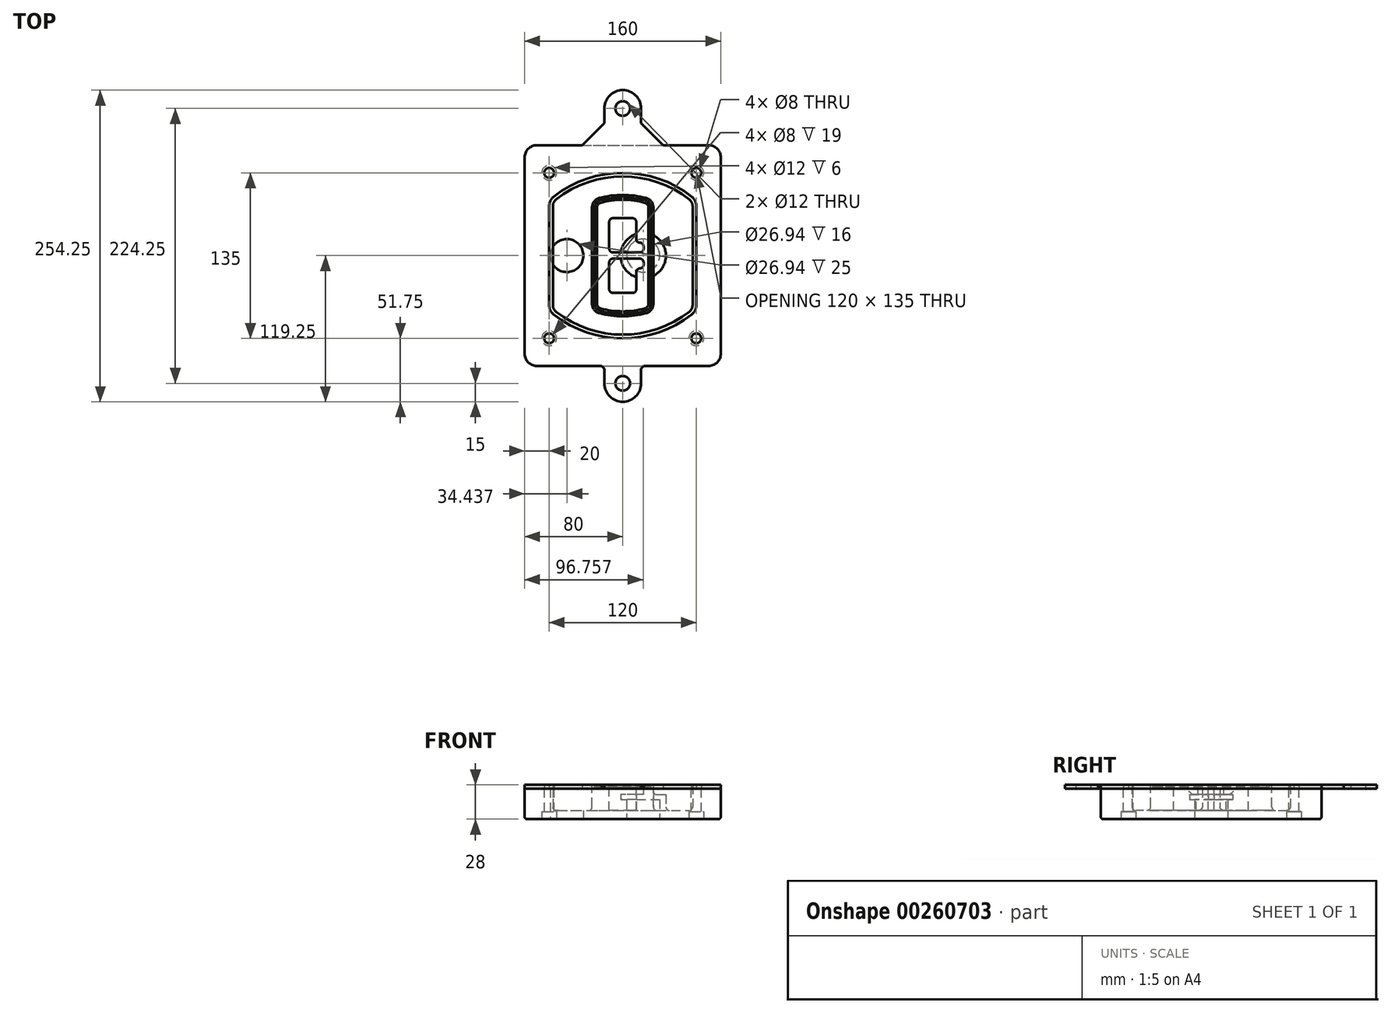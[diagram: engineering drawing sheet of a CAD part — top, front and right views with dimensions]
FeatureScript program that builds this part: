
annotation { "Feature Type Name" : "Feature", "Feature Type Description" : "" }
export const myFeature = defineFeature(function(context is Context, id is Id, definition is map)
    precondition{}
    {
        {
            var Q0;
            Q0=qCreatedBy(makeId("Top.planeOp"),FACE);
            var sketch = newSketch(context, id + "F0", { "sketchPlane" : qUnion([Q0])});
            skPoint(sketch, "E0.rect.middle", {"position": v(0, 0) * mm});
            skLineSegment(sketch, "E1.bottom", {"start": v(-70, -90) * mm, "end": v(70, -90) * mm});
            skLineSegment(sketch, "E1.top", {"start": v(-70, 90) * mm, "end": v(70, 90) * mm});
            skLineSegment(sketch, "E1.left", {"start": v(-80, -80) * mm, "end": v(-80, 80) * mm});
            skLineSegment(sketch, "E1.right", {"start": v(80, -80) * mm, "end": v(80, 80) * mm});
            skLineSegment(sketch, "E2", {"start": v(-80, 90) * mm, "end": v(80, -90) * mm, "construction": true});
            skLineSegment(sketch, "E3", {"start": v(80, 90) * mm, "end": v(-80, -90) * mm, "construction": true});
            skCircle(sketch, "E4", {"center": v(-60, 67.5) * mm, "radius": 4 * mm});
            skCircle(sketch, "E5", {"center": v(60, 67.5) * mm, "radius": 4 * mm});
            skCircle(sketch, "E6", {"center": v(60, -67.5) * mm, "radius": 4 * mm});
            skCircle(sketch, "E7", {"center": v(-60, -67.5) * mm, "radius": 4 * mm});
            skLineSegment(sketch, "E8", {"start": v(-60, 67.5) * mm, "end": v(60, 67.5) * mm, "construction": true});
            skLineSegment(sketch, "E9", {"start": v(60, 67.5) * mm, "end": v(60, -67.5) * mm, "construction": true});
            skLineSegment(sketch, "E10", {"start": v(60, -67.5) * mm, "end": v(-60, -67.5) * mm, "construction": true});
            skLineSegment(sketch, "E11", {"start": v(-60, -67.5) * mm, "end": v(-60, 67.5) * mm, "construction": true});
            skLineSegment(sketch, "E12", {"start": v(-60, 40.3) * mm, "end": v(-60, -40.3) * mm});
            skLineSegment(sketch, "E13", {"start": v(60, 40.3) * mm, "end": v(60, -40.3) * mm});
            skArc(sketch, "E14", {"start": v(56.15, 48.18) * mm, "mid": v(0, 67.5) * mm, "end": v(-56.15, 48.18) * mm});
            skArc(sketch, "E15", {"start": v(-56.15, -48.18) * mm, "mid": v(0, -67.5) * mm, "end": v(56.15, -48.18) * mm});
            skLineSegment(sketch, "E16", {"start": v(-60, 0) * mm, "end": v(60, 0) * mm, "construction": true});
            skPoint(sketch, "E17.visualSharp", {"position": v(-60, -45) * mm});
            skArc(sketch, "E17.filletArc", {"start": v(-60, -40.3) * mm, "mid": v(-58.99, -44.68) * mm, "end": v(-56.15, -48.18) * mm});
            skPoint(sketch, "E18.visualSharp", {"position": v(-60, 45) * mm});
            skArc(sketch, "E18.filletArc", {"start": v(-56.15, 48.18) * mm, "mid": v(-58.99, 44.68) * mm, "end": v(-60, 40.3) * mm});
            skPoint(sketch, "E19.visualSharp", {"position": v(60, 45) * mm});
            skArc(sketch, "E19.filletArc", {"start": v(60, 40.3) * mm, "mid": v(58.99, 44.68) * mm, "end": v(56.15, 48.18) * mm});
            skPoint(sketch, "E20.visualSharp", {"position": v(60, -45) * mm});
            skArc(sketch, "E20.filletArc", {"start": v(56.15, -48.18) * mm, "mid": v(58.99, -44.68) * mm, "end": v(60, -40.3) * mm});
            skPoint(sketch, "E21.visualSharp", {"position": v(-80, 90) * mm});
            skArc(sketch, "E21.filletArc", {"start": v(-70, 90) * mm, "mid": v(-77.07, 87.07) * mm, "end": v(-80, 80) * mm});
            skPoint(sketch, "E22.visualSharp", {"position": v(80, 90) * mm});
            skArc(sketch, "E22.filletArc", {"start": v(80, 80) * mm, "mid": v(77.07, 87.07) * mm, "end": v(70, 90) * mm});
            skPoint(sketch, "E23.visualSharp", {"position": v(80, -90) * mm});
            skArc(sketch, "E23.filletArc", {"start": v(70, -90) * mm, "mid": v(77.07, -87.07) * mm, "end": v(80, -80) * mm});
            skPoint(sketch, "E24.visualSharp", {"position": v(-80, -90) * mm});
            skArc(sketch, "E24.filletArc", {"start": v(-80, -80) * mm, "mid": v(-77.07, -87.07) * mm, "end": v(-70, -90) * mm});
            skArc(sketch, "E25.0", {"start": v(57, 40.3) * mm, "mid": v(56.3, 43.36) * mm, "end": v(54.3, 45.81) * mm});
            skLineSegment(sketch, "E25.1", {"start": v(57, 40.3) * mm, "end": v(57, -40.3) * mm});
            skArc(sketch, "E25.2", {"start": v(54.3, -45.81) * mm, "mid": v(56.3, -43.36) * mm, "end": v(57, -40.3) * mm});
            skArc(sketch, "E25.3", {"start": v(-54.3, -45.81) * mm, "mid": v(0, -64.5) * mm, "end": v(54.3, -45.81) * mm});
            skArc(sketch, "E25.4", {"start": v(-57, -40.3) * mm, "mid": v(-56.3, -43.36) * mm, "end": v(-54.3, -45.81) * mm});
            skArc(sketch, "E25.5", {"start": v(54.3, 45.81) * mm, "mid": v(0, 64.5) * mm, "end": v(-54.3, 45.81) * mm});
            skLineSegment(sketch, "E25.6", {"start": v(-57, 40.3) * mm, "end": v(-57, -40.3) * mm});
            skArc(sketch, "E25.7", {"start": v(-54.3, 45.81) * mm, "mid": v(-56.3, 43.36) * mm, "end": v(-57, 40.3) * mm});
            skArc(sketch, "E26.0", {"start": v(-58.62, 51.33) * mm, "mid": v(-62.58, 46.43) * mm, "end": v(-64, 40.3) * mm});
            skArc(sketch, "E26.1", {"start": v(58.62, 51.33) * mm, "mid": v(0, 71.5) * mm, "end": v(-58.62, 51.33) * mm});
            skArc(sketch, "E26.2", {"start": v(64, 40.3) * mm, "mid": v(62.58, 46.43) * mm, "end": v(58.62, 51.33) * mm});
            skLineSegment(sketch, "E26.3", {"start": v(64, 40.3) * mm, "end": v(64, -40.3) * mm});
            skArc(sketch, "E26.4", {"start": v(58.62, -51.33) * mm, "mid": v(62.58, -46.43) * mm, "end": v(64, -40.3) * mm});
            skLineSegment(sketch, "E26.5", {"start": v(-64, 40.3) * mm, "end": v(-64, -40.3) * mm});
            skArc(sketch, "E26.6", {"start": v(-58.62, -51.33) * mm, "mid": v(0, -71.5) * mm, "end": v(58.62, -51.33) * mm});
            skArc(sketch, "E26.7", {"start": v(-64, -40.3) * mm, "mid": v(-62.58, -46.43) * mm, "end": v(-58.62, -51.33) * mm});
            skSolve(sketch);
        }
        {
            var Q0;
            Q0=makeQuery(id+"F0.imprint","IMPRINT",FACE,{"disambiguationData":[TD([[makeQuery(id+"F0.imprint","IMPRINT",EDGE,{"derivedFrom":sQuery(id+"F0.wireOp",EDGE,"E1.bottom")}),1.0]])]});
            var Q1;
            Q1=makeQuery(id+"F0.imprint","IMPRINT",FACE,{"disambiguationData":[TD([[makeQuery(id+"F0.imprint","IMPRINT",EDGE,{"derivedFrom":sQuery(id+"F0.wireOp",EDGE,"E12")}),1.0]])]});
            var Q2;
            Q2=makeQuery(id+"F0.imprint","IMPRINT",FACE,{"disambiguationData":[TD([[makeQuery(id+"F0.imprint","IMPRINT",EDGE,{"derivedFrom":sQuery(id+"F0.wireOp",EDGE,"E25.0")}),1.0]])]});
            var Q3;
            Q3=makeQuery(id+"F0.imprint","IMPRINT",FACE,{"disambiguationData":[TD([[makeQuery(id+"F0.imprint","IMPRINT",EDGE,{"derivedFrom":sQuery(id+"F0.wireOp",EDGE,"E12")}),-1.0]])]});
            extrude(context, id + "F1", {"entities" : qUnion([Q0, Q1, Q2, Q3]), "oppositeDirection" : true, "depth" : 25 * mm});
        }
        {
            var Q0;
            Q0=makeQuery(id+"F0.imprint","IMPRINT",FACE,{"disambiguationData":[TD([[makeQuery(id+"F0.imprint","IMPRINT",EDGE,{"derivedFrom":sQuery(id+"F0.wireOp",EDGE,"E12")}),1.0]])]});
            extrude(context, id + "F2", {"entities" : qUnion([Q0]), "operationType" : NewBodyOperationType.ADD, "depth" : 3 * mm});
        }
        {
            var Q0;
            Q0=makeQuery(id+"F0.imprint","IMPRINT",FACE,{"disambiguationData":[TD([[makeQuery(id+"F0.imprint","IMPRINT",EDGE,{"derivedFrom":sQuery(id+"F0.wireOp",EDGE,"E25.0")}),1.0]])]});
            extrude(context, id + "F3", {"entities" : qUnion([Q0]), "operationType" : NewBodyOperationType.REMOVE, "oppositeDirection" : true, "depth" : 18 * mm});
        }
        {
            var Q0;
            Q0=makeQuery(id+"F2.opExtrude","CAP_FACE",FACE,{"disambiguationData":[OSD([sQuery(id+"F0.wireOp",EDGE,"E12"),sQuery(id+"F0.wireOp",EDGE,"E13"),sQuery(id+"F0.wireOp",EDGE,"E14"),sQuery(id+"F0.wireOp",EDGE,"E15"),sQuery(id+"F0.wireOp",EDGE,"E17.filletArc"),sQuery(id+"F0.wireOp",EDGE,"E18.filletArc"),sQuery(id+"F0.wireOp",EDGE,"E19.filletArc"),sQuery(id+"F0.wireOp",EDGE,"E20.filletArc"),sQuery(id+"F0.wireOp",EDGE,"E25.0"),sQuery(id+"F0.wireOp",EDGE,"E25.1"),sQuery(id+"F0.wireOp",EDGE,"E25.2"),sQuery(id+"F0.wireOp",EDGE,"E25.3"),sQuery(id+"F0.wireOp",EDGE,"E25.4"),sQuery(id+"F0.wireOp",EDGE,"E25.5"),sQuery(id+"F0.wireOp",EDGE,"E25.6"),sQuery(id+"F0.wireOp",EDGE,"E25.7")])],"isStart":false});
            var sketch = newSketch(context, id + "F4", { "sketchPlane" : qUnion([Q0])});
            skArc(sketch, "E27.0", {"start": v(-19.08, -46.97) * mm, "mid": v(0, -49.5) * mm, "end": v(19.08, -46.97) * mm});
            skArc(sketch, "E28.0", {"start": v(19.08, 46.97) * mm, "mid": v(0, 49.5) * mm, "end": v(-19.08, 46.97) * mm});
            skLineSegment(sketch, "E29", {"start": v(-25, 39.25) * mm, "end": v(-25, -39.25) * mm});
            skLineSegment(sketch, "E30", {"start": v(25, 39.25) * mm, "end": v(25, -39.25) * mm});
            skLineSegment(sketch, "E31", {"start": v(-25, 45.1) * mm, "end": v(25, 45.1) * mm, "construction": true});
            skLineSegment(sketch, "E32", {"start": v(-25, -45.1) * mm, "end": v(25, -45.1) * mm, "construction": true});
            skPoint(sketch, "E33.visualSharp", {"position": v(-25, 45.1) * mm});
            skArc(sketch, "E33.filletArc", {"start": v(-19.08, 46.97) * mm, "mid": v(-23.35, 44.11) * mm, "end": v(-25, 39.25) * mm});
            skPoint(sketch, "E34.visualSharp", {"position": v(25, 45.1) * mm});
            skArc(sketch, "E34.filletArc", {"start": v(25, 39.25) * mm, "mid": v(23.35, 44.11) * mm, "end": v(19.08, 46.97) * mm});
            skPoint(sketch, "E35.visualSharp", {"position": v(25, -45.1) * mm});
            skArc(sketch, "E35.filletArc", {"start": v(19.08, -46.97) * mm, "mid": v(23.35, -44.11) * mm, "end": v(25, -39.25) * mm});
            skPoint(sketch, "E36.visualSharp", {"position": v(-25, -45.1) * mm});
            skArc(sketch, "E36.filletArc", {"start": v(-25, -39.25) * mm, "mid": v(-23.35, -44.11) * mm, "end": v(-19.08, -46.97) * mm});
            skArc(sketch, "E37.0", {"start": v(54.3, 45.81) * mm, "mid": v(0, 64.5) * mm, "end": v(-54.3, 45.81) * mm});
            skArc(sketch, "E37.1", {"start": v(-54.3, 45.81) * mm, "mid": v(-56.3, 43.36) * mm, "end": v(-57, 40.3) * mm});
            skLineSegment(sketch, "E37.2", {"start": v(-57, 40.3) * mm, "end": v(-57, -40.3) * mm});
            skArc(sketch, "E37.3", {"start": v(-57, -40.3) * mm, "mid": v(-56.3, -43.36) * mm, "end": v(-54.3, -45.81) * mm});
            skArc(sketch, "E37.4", {"start": v(-54.3, -45.81) * mm, "mid": v(0, -64.5) * mm, "end": v(54.3, -45.81) * mm});
            skArc(sketch, "E37.5", {"start": v(54.3, -45.81) * mm, "mid": v(56.3, -43.36) * mm, "end": v(57, -40.3) * mm});
            skLineSegment(sketch, "E37.6", {"start": v(57, 40.3) * mm, "end": v(57, -40.3) * mm});
            skArc(sketch, "E37.7", {"start": v(57, 40.3) * mm, "mid": v(56.3, 43.36) * mm, "end": v(54.3, 45.81) * mm});
            skLineSegment(sketch, "E38.0", {"start": v(23, 39.25) * mm, "end": v(23, -39.25) * mm});
            skArc(sketch, "E38.1", {"start": v(18.56, -45.04) * mm, "mid": v(21.76, -42.9) * mm, "end": v(23, -39.25) * mm});
            skArc(sketch, "E38.2", {"start": v(-18.56, -45.04) * mm, "mid": v(0, -47.5) * mm, "end": v(18.56, -45.04) * mm});
            skArc(sketch, "E38.3", {"start": v(-23, -39.25) * mm, "mid": v(-21.76, -42.9) * mm, "end": v(-18.56, -45.04) * mm});
            skLineSegment(sketch, "E38.4", {"start": v(-23, 39.25) * mm, "end": v(-23, -39.25) * mm});
            skArc(sketch, "E38.5", {"start": v(23, 39.25) * mm, "mid": v(21.76, 42.9) * mm, "end": v(18.56, 45.04) * mm});
            skArc(sketch, "E38.6", {"start": v(-18.56, 45.04) * mm, "mid": v(-21.76, 42.9) * mm, "end": v(-23, 39.25) * mm});
            skArc(sketch, "E38.7", {"start": v(18.56, 45.04) * mm, "mid": v(0, 47.5) * mm, "end": v(-18.56, 45.04) * mm});
            skArc(sketch, "E39.0", {"start": v(21, 39.25) * mm, "mid": v(20.18, 41.68) * mm, "end": v(18.04, 43.1) * mm});
            skLineSegment(sketch, "E39.1", {"start": v(21, 39.25) * mm, "end": v(21, -39.25) * mm});
            skArc(sketch, "E39.2", {"start": v(18.04, -43.1) * mm, "mid": v(20.18, -41.68) * mm, "end": v(21, -39.25) * mm});
            skArc(sketch, "E39.3", {"start": v(-18.04, -43.1) * mm, "mid": v(0, -45.5) * mm, "end": v(18.04, -43.1) * mm});
            skArc(sketch, "E39.4", {"start": v(-21, -39.25) * mm, "mid": v(-20.18, -41.68) * mm, "end": v(-18.04, -43.1) * mm});
            skArc(sketch, "E39.5", {"start": v(18.04, 43.1) * mm, "mid": v(0, 45.5) * mm, "end": v(-18.04, 43.1) * mm});
            skLineSegment(sketch, "E39.6", {"start": v(-21, 39.25) * mm, "end": v(-21, -39.25) * mm});
            skArc(sketch, "E39.7", {"start": v(-18.04, 43.1) * mm, "mid": v(-20.18, 41.68) * mm, "end": v(-21, 39.25) * mm});
            skLineSegment(sketch, "E40", {"start": v(-25, 0) * mm, "end": v(25, 0) * mm, "construction": true});
            skLineSegment(sketch, "E41", {"start": v(-11, 5.5) * mm, "end": v(-11, 27.5) * mm});
            skLineSegment(sketch, "E42", {"start": v(-8, 30.5) * mm, "end": v(8, 30.5) * mm});
            skLineSegment(sketch, "E43", {"start": v(11, 27.5) * mm, "end": v(11, 13.5) * mm});
            skLineSegment(sketch, "E44", {"start": v(14, 10.5) * mm, "end": v(14, 10.5) * mm});
            skLineSegment(sketch, "E45", {"start": v(17, 7.5) * mm, "end": v(17, 5.5) * mm});
            skLineSegment(sketch, "E46", {"start": v(14, 2.5) * mm, "end": v(-8, 2.5) * mm});
            skPoint(sketch, "E47.visualSharp", {"position": v(-11, 30.5) * mm});
            skArc(sketch, "E47.filletArc", {"start": v(-8, 30.5) * mm, "mid": v(-10.12, 29.62) * mm, "end": v(-11, 27.5) * mm});
            skPoint(sketch, "E48.visualSharp", {"position": v(11, 30.5) * mm});
            skArc(sketch, "E48.filletArc", {"start": v(11, 27.5) * mm, "mid": v(10.12, 29.62) * mm, "end": v(8, 30.5) * mm});
            skPoint(sketch, "E49.visualSharp", {"position": v(11, 10.5) * mm});
            skArc(sketch, "E49.filletArc", {"start": v(11, 13.5) * mm, "mid": v(11.88, 11.38) * mm, "end": v(14, 10.5) * mm});
            skPoint(sketch, "E50.visualSharp", {"position": v(17, 10.5) * mm});
            skArc(sketch, "E50.filletArc", {"start": v(17, 7.5) * mm, "mid": v(16.12, 9.62) * mm, "end": v(14, 10.5) * mm});
            skPoint(sketch, "E51.visualSharp", {"position": v(17, 2.5) * mm});
            skArc(sketch, "E51.filletArc", {"start": v(14, 2.5) * mm, "mid": v(16.12, 3.38) * mm, "end": v(17, 5.5) * mm});
            skPoint(sketch, "E52.visualSharp", {"position": v(-11, 2.5) * mm});
            skArc(sketch, "E52.filletArc", {"start": v(-11, 5.5) * mm, "mid": v(-10.12, 3.38) * mm, "end": v(-8, 2.5) * mm});
            skLineSegment(sketch, "E53.0.MirrorCS", {"start": v(14, -2.5) * mm, "end": v(-8, -2.5) * mm});
            skArc(sketch, "E54.0.MirrorCS", {"start": v(-11, -5.5) * mm, "mid": v(-10.12, -3.38) * mm, "end": v(-8, -2.5) * mm});
            skLineSegment(sketch, "E55.0.MirrorCS", {"start": v(-11, -5.5) * mm, "end": v(-11, -27.5) * mm});
            skArc(sketch, "E56.0.MirrorCS", {"start": v(-8, -30.5) * mm, "mid": v(-10.12, -29.62) * mm, "end": v(-11, -27.5) * mm});
            skLineSegment(sketch, "E57.0.MirrorCS", {"start": v(-8, -30.5) * mm, "end": v(8, -30.5) * mm});
            skArc(sketch, "E58.0.MirrorCS", {"start": v(11, -27.5) * mm, "mid": v(10.12, -29.62) * mm, "end": v(8, -30.5) * mm});
            skLineSegment(sketch, "E59.0.MirrorCS", {"start": v(11, -27.5) * mm, "end": v(11, -13.5) * mm});
            skArc(sketch, "E60.0.MirrorCS", {"start": v(11, -13.5) * mm, "mid": v(11.88, -11.38) * mm, "end": v(14, -10.5) * mm});
            skArc(sketch, "E61.0.MirrorCS", {"start": v(17, -7.5) * mm, "mid": v(16.12, -9.62) * mm, "end": v(14, -10.5) * mm});
            skLineSegment(sketch, "E62.0.MirrorCS", {"start": v(17, -7.5) * mm, "end": v(17, -5.5) * mm});
            skArc(sketch, "E63.0.MirrorCS", {"start": v(14, -2.5) * mm, "mid": v(16.12, -3.38) * mm, "end": v(17, -5.5) * mm});
            skSolve(sketch);
        }
        {
            var Q0;
            Q0=makeQuery(id+"F4.imprint","IMPRINT",FACE,{"disambiguationData":[TD([[makeQuery(id+"F4.imprint","IMPRINT",EDGE,{"derivedFrom":sQuery(id+"F4.wireOp",EDGE,"E27.0")}),1.0]])]});
            var Q1;
            Q1=makeQuery(id+"F4.imprint","IMPRINT",FACE,{"disambiguationData":[TD([[makeQuery(id+"F4.imprint","IMPRINT",EDGE,{"derivedFrom":sQuery(id+"F4.wireOp",EDGE,"E38.0")}),-1.0]])]});
            var Q2;
            Q2=makeQuery(id+"F4.imprint","IMPRINT",FACE,{"disambiguationData":[TD([[makeQuery(id+"F4.imprint","IMPRINT",EDGE,{"derivedFrom":sQuery(id+"F4.wireOp",EDGE,"E39.0")}),1.0]])]});
            extrude(context, id + "F5", {"entities" : qUnion([Q0, Q1, Q2]), "operationType" : NewBodyOperationType.ADD, "endBound" : BoundingType.UP_TO_NEXT, "oppositeDirection" : true, "depth" : 25 * mm});
        }
        {
            var Q0;
            Q0=makeQuery(id+"F4.imprint","IMPRINT",FACE,{"disambiguationData":[TD([[makeQuery(id+"F4.imprint","IMPRINT",EDGE,{"derivedFrom":sQuery(id+"F4.wireOp",EDGE,"E38.0")}),-1.0]])]});
            extrude(context, id + "F6", {"entities" : qUnion([Q0]), "operationType" : NewBodyOperationType.REMOVE, "oppositeDirection" : true, "depth" : 2 * mm});
        }
        {
            var Q0;
            Q0=makeQuery(id+"F1.opExtrude","CAP_FACE",FACE,{"disambiguationData":[OSD([sQuery(id+"F0.wireOp",EDGE,"E1.bottom"),sQuery(id+"F0.wireOp",EDGE,"E1.top"),sQuery(id+"F0.wireOp",EDGE,"E1.left"),sQuery(id+"F0.wireOp",EDGE,"E1.right"),sQuery(id+"F0.wireOp",EDGE,"E4"),sQuery(id+"F0.wireOp",EDGE,"E5"),sQuery(id+"F0.wireOp",EDGE,"E6"),sQuery(id+"F0.wireOp",EDGE,"E7"),sQuery(id+"F0.wireOp",EDGE,"E21.filletArc"),sQuery(id+"F0.wireOp",EDGE,"E22.filletArc"),sQuery(id+"F0.wireOp",EDGE,"E23.filletArc"),sQuery(id+"F0.wireOp",EDGE,"E24.filletArc")])],"isStart":false});
            var sketch = newSketch(context, id + "F7", { "sketchPlane" : qUnion([Q0])});
            skCircle(sketch, "E64", {"center": v(16.76, 0) * mm, "radius": 13.47 * mm});
            skCircle(sketch, "E65", {"center": v(-45.56, 0) * mm, "radius": 13.47 * mm});
            skLineSegment(sketch, "E66", {"start": v(80, 0) * mm, "end": v(-80, 0) * mm});
            skCircle(sketch, "E67", {"center": v(16.76, 0) * mm, "radius": 18.47 * mm});
            skCircle(sketch, "E68", {"center": v(60, -67.5) * mm, "radius": 6 * mm});
            skCircle(sketch, "E69", {"center": v(-60, -67.5) * mm, "radius": 6 * mm});
            skCircle(sketch, "E70", {"center": v(-60, 67.5) * mm, "radius": 6 * mm});
            skCircle(sketch, "E71", {"center": v(60, 67.5) * mm, "radius": 6 * mm});
            skSolve(sketch);
        }
        {
            var Q0;
            {var subQ1=sQuery(id+"F7.wireOp",EDGE,"E66");var subQ4=sQuery(id+"F7.wireOp",EDGE,"E64");var subQ6=makeQuery(id+"F7.imprint","INTERSECT",VERTEX,{"disambiguationData":[OD(0.0)],"derivedFrom":[subQ4,subQ1]});Q0=makeQuery(id+"F7.imprint","IMPRINT",FACE,{"disambiguationData":[TD([[makeQuery(id+"F7.imprint","IMPRINT",EDGE,{"disambiguationData":[TD([[subQ6,-1.0]])],"derivedFrom":subQ4}),-1.0]])]});}
            var Q1;
            {var subQ0=sQuery(id+"F7.wireOp",EDGE,"E66");var subQ1=sQuery(id+"F7.wireOp",EDGE,"E64");var subQ3=makeQuery(id+"F7.imprint","INTERSECT",VERTEX,{"disambiguationData":[OD(0.0)],"derivedFrom":[subQ1,subQ0]});Q1=makeQuery(id+"F7.imprint","IMPRINT",FACE,{"disambiguationData":[TD([[makeQuery(id+"F7.imprint","IMPRINT",EDGE,{"disambiguationData":[TD([[subQ3,-1.0]])],"derivedFrom":subQ1}),1.0]])]});}
            var Q2;
            {var subQ0=sQuery(id+"F7.wireOp",EDGE,"E66");var subQ1=sQuery(id+"F7.wireOp",EDGE,"E64");var subQ3=makeQuery(id+"F7.imprint","INTERSECT",VERTEX,{"disambiguationData":[OD(0.0)],"derivedFrom":[subQ1,subQ0]});Q2=makeQuery(id+"F7.imprint","IMPRINT",FACE,{"disambiguationData":[TD([[makeQuery(id+"F7.imprint","IMPRINT",EDGE,{"disambiguationData":[TD([[subQ3,1.0]])],"derivedFrom":subQ1}),1.0]])]});}
            var Q3;
            {var subQ1=sQuery(id+"F7.wireOp",EDGE,"E66");var subQ4=sQuery(id+"F7.wireOp",EDGE,"E64");var subQ6=makeQuery(id+"F7.imprint","INTERSECT",VERTEX,{"disambiguationData":[OD(0.0)],"derivedFrom":[subQ4,subQ1]});Q3=makeQuery(id+"F7.imprint","IMPRINT",FACE,{"disambiguationData":[TD([[makeQuery(id+"F7.imprint","IMPRINT",EDGE,{"disambiguationData":[TD([[subQ6,1.0]])],"derivedFrom":subQ4}),-1.0]])]});}
            extrude(context, id + "F8", {"entities" : qUnion([Q0, Q1, Q2, Q3]), "operationType" : NewBodyOperationType.ADD, "oppositeDirection" : true, "depth" : 20 * mm});
        }
        {
            var Q0;
            {var subQ0=sQuery(id+"F7.wireOp",EDGE,"E66");var subQ1=sQuery(id+"F7.wireOp",EDGE,"E64");var subQ3=makeQuery(id+"F7.imprint","INTERSECT",VERTEX,{"disambiguationData":[OD(0.0)],"derivedFrom":[subQ1,subQ0]});Q0=makeQuery(id+"F7.imprint","IMPRINT",FACE,{"disambiguationData":[TD([[makeQuery(id+"F7.imprint","IMPRINT",EDGE,{"disambiguationData":[TD([[subQ3,-1.0]])],"derivedFrom":subQ1}),1.0]])]});}
            var Q1;
            {var subQ0=sQuery(id+"F7.wireOp",EDGE,"E66");var subQ1=sQuery(id+"F7.wireOp",EDGE,"E64");var subQ3=makeQuery(id+"F7.imprint","INTERSECT",VERTEX,{"disambiguationData":[OD(0.0)],"derivedFrom":[subQ1,subQ0]});Q1=makeQuery(id+"F7.imprint","IMPRINT",FACE,{"disambiguationData":[TD([[makeQuery(id+"F7.imprint","IMPRINT",EDGE,{"disambiguationData":[TD([[subQ3,1.0]])],"derivedFrom":subQ1}),1.0]])]});}
            extrude(context, id + "F9", {"entities" : qUnion([Q0, Q1]), "operationType" : NewBodyOperationType.REMOVE, "oppositeDirection" : true, "depth" : 16 * mm});
        }
        {
            var Q0;
            {var subQ0=sQuery(id+"F7.wireOp",EDGE,"E66");var subQ1=sQuery(id+"F7.wireOp",EDGE,"E65");var subQ3=makeQuery(id+"F7.imprint","INTERSECT",VERTEX,{"disambiguationData":[OD(0.0)],"derivedFrom":[subQ1,subQ0]});Q0=makeQuery(id+"F7.imprint","IMPRINT",FACE,{"disambiguationData":[TD([[makeQuery(id+"F7.imprint","IMPRINT",EDGE,{"disambiguationData":[TD([[subQ3,-1.0]])],"derivedFrom":subQ1}),1.0]])]});}
            var Q1;
            {var subQ0=sQuery(id+"F7.wireOp",EDGE,"E66");var subQ1=sQuery(id+"F7.wireOp",EDGE,"E65");var subQ3=makeQuery(id+"F7.imprint","INTERSECT",VERTEX,{"disambiguationData":[OD(0.0)],"derivedFrom":[subQ1,subQ0]});Q1=makeQuery(id+"F7.imprint","IMPRINT",FACE,{"disambiguationData":[TD([[makeQuery(id+"F7.imprint","IMPRINT",EDGE,{"disambiguationData":[TD([[subQ3,1.0]])],"derivedFrom":subQ1}),1.0]])]});}
            extrude(context, id + "F10", {"entities" : qUnion([Q0, Q1]), "operationType" : NewBodyOperationType.REMOVE, "oppositeDirection" : true, "depth" : 25 * mm});
        }
        {
            var Q0;
            Q0=makeQuery(id+"F7.imprint","IMPRINT",FACE,{"disambiguationData":[TD([[makeQuery(id+"F7.imprint","IMPRINT",EDGE,{"derivedFrom":sQuery(id+"F7.wireOp",EDGE,"E68")}),1.0]])]});
            var Q1;
            Q1=makeQuery(id+"F7.imprint","IMPRINT",FACE,{"disambiguationData":[TD([[makeQuery(id+"F7.imprint","IMPRINT",EDGE,{"derivedFrom":makeQuery(id+"F1.opExtrude","CAP_EDGE",EDGE,{"disambiguationData":[OSD([sQuery(id+"F0.wireOp",EDGE,"E5")])],"isStart":false})}),-1.0]])]});
            var Q2;
            Q2=makeQuery(id+"F7.imprint","IMPRINT",FACE,{"disambiguationData":[TD([[makeQuery(id+"F7.imprint","IMPRINT",EDGE,{"derivedFrom":sQuery(id+"F7.wireOp",EDGE,"E69")}),1.0]])]});
            var Q3;
            Q3=makeQuery(id+"F7.imprint","IMPRINT",FACE,{"disambiguationData":[TD([[makeQuery(id+"F7.imprint","IMPRINT",EDGE,{"derivedFrom":makeQuery(id+"F1.opExtrude","CAP_EDGE",EDGE,{"disambiguationData":[OSD([sQuery(id+"F0.wireOp",EDGE,"E4")])],"isStart":false})}),-1.0]])]});
            var Q4;
            Q4=makeQuery(id+"F7.imprint","IMPRINT",FACE,{"disambiguationData":[TD([[makeQuery(id+"F7.imprint","IMPRINT",EDGE,{"derivedFrom":sQuery(id+"F7.wireOp",EDGE,"E70")}),1.0]])]});
            var Q5;
            Q5=makeQuery(id+"F7.imprint","IMPRINT",FACE,{"disambiguationData":[TD([[makeQuery(id+"F7.imprint","IMPRINT",EDGE,{"derivedFrom":makeQuery(id+"F1.opExtrude","CAP_EDGE",EDGE,{"disambiguationData":[OSD([sQuery(id+"F0.wireOp",EDGE,"E7")])],"isStart":false})}),-1.0]])]});
            var Q6;
            Q6=makeQuery(id+"F7.imprint","IMPRINT",FACE,{"disambiguationData":[TD([[makeQuery(id+"F7.imprint","IMPRINT",EDGE,{"derivedFrom":sQuery(id+"F7.wireOp",EDGE,"E71")}),1.0]])]});
            var Q7;
            Q7=makeQuery(id+"F7.imprint","IMPRINT",FACE,{"disambiguationData":[TD([[makeQuery(id+"F7.imprint","IMPRINT",EDGE,{"derivedFrom":makeQuery(id+"F1.opExtrude","CAP_EDGE",EDGE,{"disambiguationData":[OSD([sQuery(id+"F0.wireOp",EDGE,"E6")])],"isStart":false})}),-1.0]])]});
            extrude(context, id + "F11", {"entities" : qUnion([Q0, Q1, Q2, Q3, Q4, Q5, Q6, Q7]), "operationType" : NewBodyOperationType.REMOVE, "oppositeDirection" : true, "depth" : 6 * mm});
        }
        {
            var Q0;
            Q0=makeQuery(id+"F9.boolean.opBoolean","COPY",FACE,{"derivedFrom":makeQuery(id+"F9.opExtrude","CAP_FACE",FACE,{"disambiguationData":[OSD([sQuery(id+"F7.wireOp",EDGE,"E64")])],"isStart":false})});
            var sketch = newSketch(context, id + "F12", { "sketchPlane" : qUnion([Q0])});
            skArc(sketch, "E72.0", {"start": v(11, 17.55) * mm, "mid": v(2.57, 11.82) * mm, "end": v(-1.54, 2.5) * mm});
            skArc(sketch, "E72.1", {"start": v(-1.54, -2.5) * mm, "mid": v(2.57, -11.82) * mm, "end": v(11, -17.55) * mm});
            skLineSegment(sketch, "E73", {"start": v(-1.54, -2.5) * mm, "end": v(14, -2.5) * mm});
            skLineSegment(sketch, "E74.0", {"start": v(14, 2.5) * mm, "end": v(-1.54, 2.5) * mm});
            skArc(sketch, "E74.1", {"start": v(14, 2.5) * mm, "mid": v(16.12, 3.38) * mm, "end": v(17, 5.5) * mm});
            skLineSegment(sketch, "E74.2", {"start": v(17, 7.5) * mm, "end": v(17, 5.5) * mm});
            skArc(sketch, "E74.3", {"start": v(17, 7.5) * mm, "mid": v(16.12, 9.62) * mm, "end": v(14, 10.5) * mm});
            skArc(sketch, "E74.4", {"start": v(11, 13.5) * mm, "mid": v(11.88, 11.38) * mm, "end": v(14, 10.5) * mm});
            skLineSegment(sketch, "E74.5", {"start": v(11, 17.55) * mm, "end": v(11, 13.5) * mm});
            skLineSegment(sketch, "E74.7", {"start": v(14, -2.5) * mm, "end": v(-1.54, -2.5) * mm});
            skArc(sketch, "E74.8", {"start": v(14, -2.5) * mm, "mid": v(16.12, -3.38) * mm, "end": v(17, -5.5) * mm});
            skLineSegment(sketch, "E74.9", {"start": v(17, -7.5) * mm, "end": v(17, -5.5) * mm});
            skArc(sketch, "E74.10", {"start": v(17, -7.5) * mm, "mid": v(16.12, -9.62) * mm, "end": v(14, -10.5) * mm});
            skArc(sketch, "E74.11", {"start": v(11, -13.5) * mm, "mid": v(11.88, -11.38) * mm, "end": v(14, -10.5) * mm});
            skLineSegment(sketch, "E74.12", {"start": v(11, -17.55) * mm, "end": v(11, -13.5) * mm});
            skPoint(sketch, "E75.orphan", {"position": v(11, -27.5) * mm});
            skPoint(sketch, "E76.orphan", {"position": v(-8, -2.5) * mm});
            skPoint(sketch, "E77.orphan", {"position": v(-8, 2.5) * mm});
            skPoint(sketch, "E78.orphan", {"position": v(11, 27.5) * mm});
            skSolve(sketch);
        }
        {
            var Q0;
            {var subQ7=sQuery(id+"F12.wireOp",EDGE,"E72.0");var subQ14=sQuery(id+"F12.wireOp",EDGE,"E72.1");var subQ16=sQuery(id+"F12.wireOp",EDGE,"E74.1");var subQ18=sQuery(id+"F12.wireOp",EDGE,"E74.8");Q0=qUnion([makeQuery(id+"F12.imprint","IMPRINT",FACE,{"disambiguationData":[TD([[makeQuery(id+"F12.imprint","IMPRINT",EDGE,{"derivedFrom":subQ7}),1.0]])]}),makeQuery(id+"F12.imprint","IMPRINT",FACE,{"disambiguationData":[TD([[makeQuery(id+"F12.imprint","IMPRINT",EDGE,{"derivedFrom":subQ14}),1.0]])]}),makeQuery(id+"F12.imprint","IMPRINT",FACE,{"disambiguationData":[TD([[makeQuery(id+"F12.imprint","IMPRINT",EDGE,{"derivedFrom":subQ16}),1.0]])]}),makeQuery(id+"F12.imprint","IMPRINT",FACE,{"disambiguationData":[TD([[makeQuery(id+"F12.imprint","IMPRINT",EDGE,{"derivedFrom":subQ18}),-1.0]])]})]);}
            var Q1;
            Q1=makeQuery(id+"F5.boolean.opBoolean","SPLIT",FACE,{"disambiguationData":[TD([makeQuery(id+"F5.opExtrude","SWEPT_FACE",FACE,{"disambiguationData":[OSD([sQuery(id+"F4.wireOp",EDGE,"E41")])]})])],"derivedFrom":makeQuery(id+"F3.boolean.opBoolean","COPY",FACE,{"derivedFrom":makeQuery(id+"F3.opExtrude","CAP_FACE",FACE,{"disambiguationData":[OSD([sQuery(id+"F0.wireOp",EDGE,"E25.0"),sQuery(id+"F0.wireOp",EDGE,"E25.1"),sQuery(id+"F0.wireOp",EDGE,"E25.2"),sQuery(id+"F0.wireOp",EDGE,"E25.3"),sQuery(id+"F0.wireOp",EDGE,"E25.4"),sQuery(id+"F0.wireOp",EDGE,"E25.5"),sQuery(id+"F0.wireOp",EDGE,"E25.6"),sQuery(id+"F0.wireOp",EDGE,"E25.7")])],"isStart":false})})});
            extrude(context, id + "F13", {"entities" : qUnion([Q0]), "operationType" : NewBodyOperationType.REMOVE, "endBound" : BoundingType.UP_TO_SURFACE, "endBoundEntityFace" : qUnion([Q1]), "depth" : 25 * mm});
        }
        {
            var Q0;
            Q0=makeQuery(id+"F3.boolean.opBoolean","COPY",EDGE,{"derivedFrom":makeQuery(id+"F3.opExtrude","CAP_EDGE",EDGE,{"disambiguationData":[OSD([sQuery(id+"F0.wireOp",EDGE,"E25.6")])],"isStart":false})});
            var Q1;
            Q1=makeQuery(id+"F8.boolean.opBoolean","INTERSECT",EDGE,{"derivedFrom":[makeQuery(id+"F5.opExtrude","SWEPT_FACE",FACE,{"disambiguationData":[OSD([sQuery(id+"F4.wireOp",EDGE,"E30")])]}),makeQuery(id+"F8.opExtrude","CAP_FACE",FACE,{"disambiguationData":[OSD([sQuery(id+"F7.wireOp",EDGE,"E67")])],"isStart":false})]});
            var Q2;
            Q2=makeQuery(id+"F8.boolean.opBoolean","INTERSECT",EDGE,{"disambiguationData":[OD(1.0)],"derivedFrom":[makeQuery(id+"F5.opExtrude","SWEPT_FACE",FACE,{"disambiguationData":[OSD([sQuery(id+"F4.wireOp",EDGE,"E30")])]}),makeQuery(id+"F8.opExtrude","SWEPT_FACE",FACE,{"disambiguationData":[OSD([sQuery(id+"F7.wireOp",EDGE,"E67")])]})]});
            var Q3;
            {var subQ0=sQuery(id+"F4.wireOp",EDGE,"E30");Q3=makeQuery(id+"F8.boolean.opBoolean","SPLIT",EDGE,{"disambiguationData":[TD([makeQuery(id+"F5.opExtrude","SWEPT_FACE",FACE,{"disambiguationData":[OSD([sQuery(id+"F4.wireOp",EDGE,"E35.filletArc")])]})])],"derivedFrom":makeQuery(id+"F5.opExtrude","CAP_EDGE",EDGE,{"disambiguationData":[OSD([subQ0])],"isStart":false})});}
            var Q4;
            {var subQ0=sQuery(id+"F0.wireOp",EDGE,"E25.7");var subQ1=sQuery(id+"F0.wireOp",EDGE,"E25.1");var subQ2=sQuery(id+"F0.wireOp",EDGE,"E25.6");var subQ3=sQuery(id+"F0.wireOp",EDGE,"E25.5");var subQ4=sQuery(id+"F0.wireOp",EDGE,"E25.4");var subQ5=sQuery(id+"F0.wireOp",EDGE,"E25.0");var subQ6=sQuery(id+"F0.wireOp",EDGE,"E25.2");var subQ7=sQuery(id+"F0.wireOp",EDGE,"E25.3");Q4=makeQuery(id+"F8.boolean.opBoolean","INTERSECT",EDGE,{"derivedFrom":[makeQuery(id+"F5.boolean.opBoolean","SPLIT",FACE,{"disambiguationData":[TD([makeQuery(id+"F2.opExtrude","SWEPT_FACE",FACE,{"disambiguationData":[OSD([subQ5])]})])],"derivedFrom":makeQuery(id+"F3.boolean.opBoolean","COPY",FACE,{"derivedFrom":makeQuery(id+"F3.opExtrude","CAP_FACE",FACE,{"disambiguationData":[OSD([subQ5,subQ1,subQ6,subQ7,subQ4,subQ3,subQ2,subQ0])],"isStart":false})})}),makeQuery(id+"F8.opExtrude","SWEPT_FACE",FACE,{"disambiguationData":[OSD([sQuery(id+"F7.wireOp",EDGE,"E67")])]})]});}
            var Q5;
            Q5=makeQuery(id+"F8.boolean.opBoolean","INTERSECT",EDGE,{"disambiguationData":[OD(0.0)],"derivedFrom":[makeQuery(id+"F5.opExtrude","SWEPT_FACE",FACE,{"disambiguationData":[OSD([sQuery(id+"F4.wireOp",EDGE,"E30")])]}),makeQuery(id+"F8.opExtrude","SWEPT_FACE",FACE,{"disambiguationData":[OSD([sQuery(id+"F7.wireOp",EDGE,"E67")])]})]});
            fillet(context, id + "F14", {"entities" : qUnion([Q0, Q1, Q2, Q3, Q4, Q5]), "radius" : 3 * mm, "tangentPropagation" : true, "allowEdgeOverflow" : false});
        }
        {
            var Q0;
            Q0=makeQuery(id+"F1.opExtrude","CAP_EDGE",EDGE,{"disambiguationData":[OSD([sQuery(id+"F0.wireOp",EDGE,"E1.bottom")])],"isStart":false});
            fillet(context, id + "F15", {"entities" : qUnion([Q0]), "radius" : 2 * mm, "tangentPropagation" : true, "allowEdgeOverflow" : false});
        }
        {
            var Q0;
            {var subQ0=sQuery(id+"F0.wireOp",EDGE,"E22.filletArc");var subQ1=sQuery(id+"F0.wireOp",EDGE,"E7");var subQ2=sQuery(id+"F0.wireOp",EDGE,"E6");var subQ3=sQuery(id+"F0.wireOp",EDGE,"E5");var subQ4=sQuery(id+"F0.wireOp",EDGE,"E4");var subQ5=sQuery(id+"F0.wireOp",EDGE,"E1.bottom");var subQ6=sQuery(id+"F0.wireOp",EDGE,"E21.filletArc");var subQ7=sQuery(id+"F0.wireOp",EDGE,"E1.top");var subQ8=sQuery(id+"F0.wireOp",EDGE,"E1.left");var subQ9=sQuery(id+"F0.wireOp",EDGE,"E1.right");var subQ10=sQuery(id+"F0.wireOp",EDGE,"E23.filletArc");var subQ11=sQuery(id+"F0.wireOp",EDGE,"E24.filletArc");Q0=makeQuery(id+"F2.boolean.opBoolean","SPLIT",FACE,{"disambiguationData":[TD([makeQuery(id+"F1.opExtrude","SWEPT_FACE",FACE,{"disambiguationData":[OSD([subQ5])]})])],"derivedFrom":makeQuery(id+"F1.opExtrude","CAP_FACE",FACE,{"disambiguationData":[OSD([subQ5,subQ7,subQ8,subQ9,subQ4,subQ3,subQ2,subQ1,subQ6,subQ0,subQ10,subQ11])],"isStart":true})});}
            var sketch = newSketch(context, id + "F16", { "sketchPlane" : qUnion([Q0])});
            skCircle(sketch, "E79", {"center": v(0, 120) * mm, "radius": 6 * mm});
            skArc(sketch, "E80", {"start": v(-15, 120) * mm, "mid": v(0, 135) * mm, "end": v(15, 120) * mm});
            skLineSegment(sketch, "E81", {"start": v(-15, 120) * mm, "end": v(-15, 108) * mm});
            skLineSegment(sketch, "E82", {"start": v(15, 120) * mm, "end": v(15, 108) * mm});
            skLineSegment(sketch, "E83", {"start": v(15, 108) * mm, "end": v(33, 90) * mm});
            skLineSegment(sketch, "E84", {"start": v(-15, 108) * mm, "end": v(-33, 90) * mm});
            skPoint(sketch, "E85.endSnap0", {"position": v(60, 0) * mm});
            skLineSegment(sketch, "E86.MirrorCS", {"start": v(15, -92.25) * mm, "end": v(33, -74.25) * mm});
            skLineSegment(sketch, "E87.MirrorCS", {"start": v(15, -104.25) * mm, "end": v(15, -92.25) * mm});
            skArc(sketch, "E88.MirrorCS", {"start": v(-15, -104.25) * mm, "mid": v(0, -119.25) * mm, "end": v(15, -104.25) * mm});
            skLineSegment(sketch, "E89.MirrorCS", {"start": v(-15, -104.25) * mm, "end": v(-15, -92.25) * mm});
            skLineSegment(sketch, "E90.MirrorCS", {"start": v(-15, -92.25) * mm, "end": v(-33, -74.25) * mm});
            skCircle(sketch, "E91.MirrorC", {"center": v(0, -104.25) * mm, "radius": 6 * mm});
            skSolve(sketch);
        }
        {
            var Q0;
            Q0=makeQuery(id+"F16.imprint","IMPRINT",FACE,{"disambiguationData":[TD([[makeQuery(id+"F16.imprint","IMPRINT",EDGE,{"derivedFrom":sQuery(id+"F16.wireOp",EDGE,"E79")}),-1.0]])]});
            var Q1;
            {var subQ0=sQuery(id+"F16.wireOp",EDGE,"E86.MirrorCS");Q1=makeQuery(id+"F16.imprint","IMPRINT",FACE,{"disambiguationData":[TD([[makeQuery(id+"F16.imprint","IMPRINT",EDGE,{"derivedFrom":subQ0}),1.0]])]});}
            var Q2;
            Q2=makeQuery(id+"F16.imprint","IMPRINT",FACE,{"disambiguationData":[TD([[makeQuery(id+"F16.imprint","IMPRINT",EDGE,{"derivedFrom":makeQuery(id+"F1.opExtrude","CAP_EDGE",EDGE,{"disambiguationData":[OSD([sQuery(id+"F0.wireOp",EDGE,"E1.left")])],"isStart":true})}),-1.0]])]});
            var Q3;
            Q3=makeQuery(id+"F2.opExtrude","CAP_FACE",FACE,{"disambiguationData":[OSD([sQuery(id+"F0.wireOp",EDGE,"E12"),sQuery(id+"F0.wireOp",EDGE,"E13"),sQuery(id+"F0.wireOp",EDGE,"E14"),sQuery(id+"F0.wireOp",EDGE,"E15"),sQuery(id+"F0.wireOp",EDGE,"E17.filletArc"),sQuery(id+"F0.wireOp",EDGE,"E18.filletArc"),sQuery(id+"F0.wireOp",EDGE,"E19.filletArc"),sQuery(id+"F0.wireOp",EDGE,"E20.filletArc"),sQuery(id+"F0.wireOp",EDGE,"E25.0"),sQuery(id+"F0.wireOp",EDGE,"E25.1"),sQuery(id+"F0.wireOp",EDGE,"E25.2"),sQuery(id+"F0.wireOp",EDGE,"E25.3"),sQuery(id+"F0.wireOp",EDGE,"E25.4"),sQuery(id+"F0.wireOp",EDGE,"E25.5"),sQuery(id+"F0.wireOp",EDGE,"E25.6"),sQuery(id+"F0.wireOp",EDGE,"E25.7")])],"isStart":false});
            extrude(context, id + "F17", {"entities" : qUnion([Q0, Q1, Q2]), "endBound" : BoundingType.UP_TO_SURFACE, "endBoundEntityFace" : qUnion([Q3]), "depth" : 25 * mm});
        }
    });
